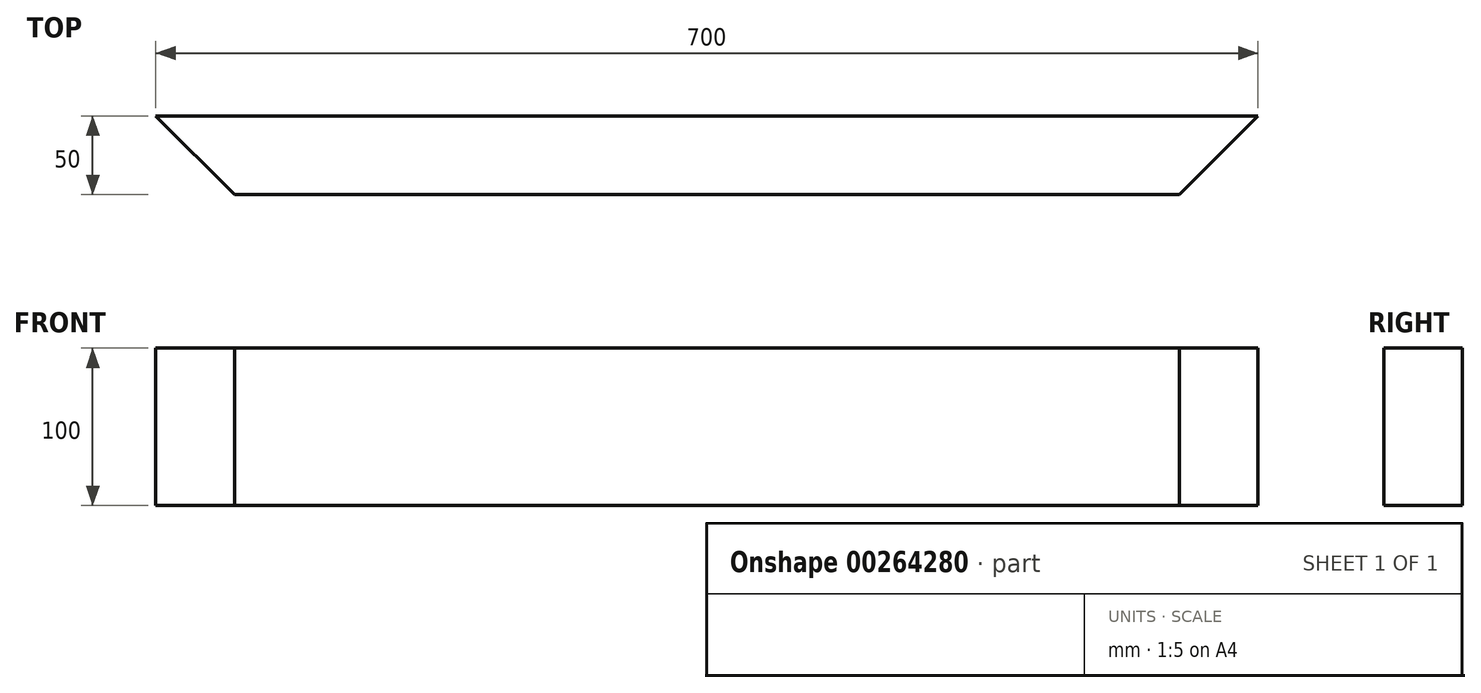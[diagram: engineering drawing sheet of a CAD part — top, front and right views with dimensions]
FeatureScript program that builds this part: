
annotation { "Feature Type Name" : "Feature", "Feature Type Description" : "" }
export const myFeature = defineFeature(function(context is Context, id is Id, definition is map)
    precondition{}
    {
        {
            var Q0;
            Q0=qCreatedBy(makeId("Front.planeOp"),FACE);
            var sketch = newSketch(context, id + "F0", { "sketchPlane" : qUnion([Q0])});
            skLineSegment(sketch, "E0.bottom", {"start": v(-350, 50) * mm, "end": v(350, 50) * mm});
            skLineSegment(sketch, "E0.top", {"start": v(-350, -50) * mm, "end": v(350, -50) * mm});
            skLineSegment(sketch, "E0.left", {"start": v(-350, 50) * mm, "end": v(-350, -50) * mm});
            skLineSegment(sketch, "E0.right", {"start": v(350, 50) * mm, "end": v(350, -50) * mm});
            skLineSegment(sketch, "E1", {"start": v(-350, 0) * mm, "end": v(350, 0) * mm, "construction": true});
            skLineSegment(sketch, "E2", {"start": v(0, 50) * mm, "end": v(0, -50) * mm, "construction": true});
            skSolve(sketch);
        }
        {
            var Q0;
            Q0=makeQuery(id+"F0.imprint","IMPRINT",FACE,{"disambiguationData":[TD([[makeQuery(id+"F0.imprint","IMPRINT",EDGE,{"derivedFrom":sQuery(id+"F0.wireOp",EDGE,"E0.bottom")}),-1.0]])]});
            extrude(context, id + "F1", {"entities" : qUnion([Q0]), "endBound" : BoundingType.SYMMETRIC, "depth" : 50 * mm});
        }
        {
            var Q0;
            Q0=makeQuery(id+"F1.opExtrude","SWEPT_FACE",FACE,{"disambiguationData":[OSD([sQuery(id+"F0.wireOp",EDGE,"E0.bottom")])]});
            var sketch = newSketch(context, id + "F2", { "sketchPlane" : qUnion([Q0])});
            skLineSegment(sketch, "E3", {"start": v(-350, 25) * mm, "end": v(-300, -25) * mm});
            skLineSegment(sketch, "E4", {"start": v(-300, -25) * mm, "end": v(-350, -25) * mm});
            skLineSegment(sketch, "E5", {"start": v(-350, -25) * mm, "end": v(-350, 25) * mm});
            skLineSegment(sketch, "E6", {"start": v(350, 25) * mm, "end": v(350, -25) * mm});
            skLineSegment(sketch, "E7", {"start": v(350, -25) * mm, "end": v(300, -25) * mm});
            skLineSegment(sketch, "E8", {"start": v(300, -25) * mm, "end": v(350, 25) * mm});
            skSolve(sketch);
        }
        {
            var Q0;
            Q0=makeQuery(id+"F2.imprint","IMPRINT",FACE,{"disambiguationData":[TD([[makeQuery(id+"F2.imprint","IMPRINT",EDGE,{"derivedFrom":sQuery(id+"F2.wireOp",EDGE,"E3")}),-1.0]])]});
            var Q1;
            Q1=makeQuery(id+"F2.imprint","IMPRINT",FACE,{"disambiguationData":[TD([[makeQuery(id+"F2.imprint","IMPRINT",EDGE,{"derivedFrom":sQuery(id+"F2.wireOp",EDGE,"E6")}),1.0]])]});
            extrude(context, id + "F3", {"entities" : qUnion([Q0, Q1]), "operationType" : NewBodyOperationType.REMOVE, "endBound" : BoundingType.THROUGH_ALL, "oppositeDirection" : true, "depth" : 25 * mm});
        }
    });
